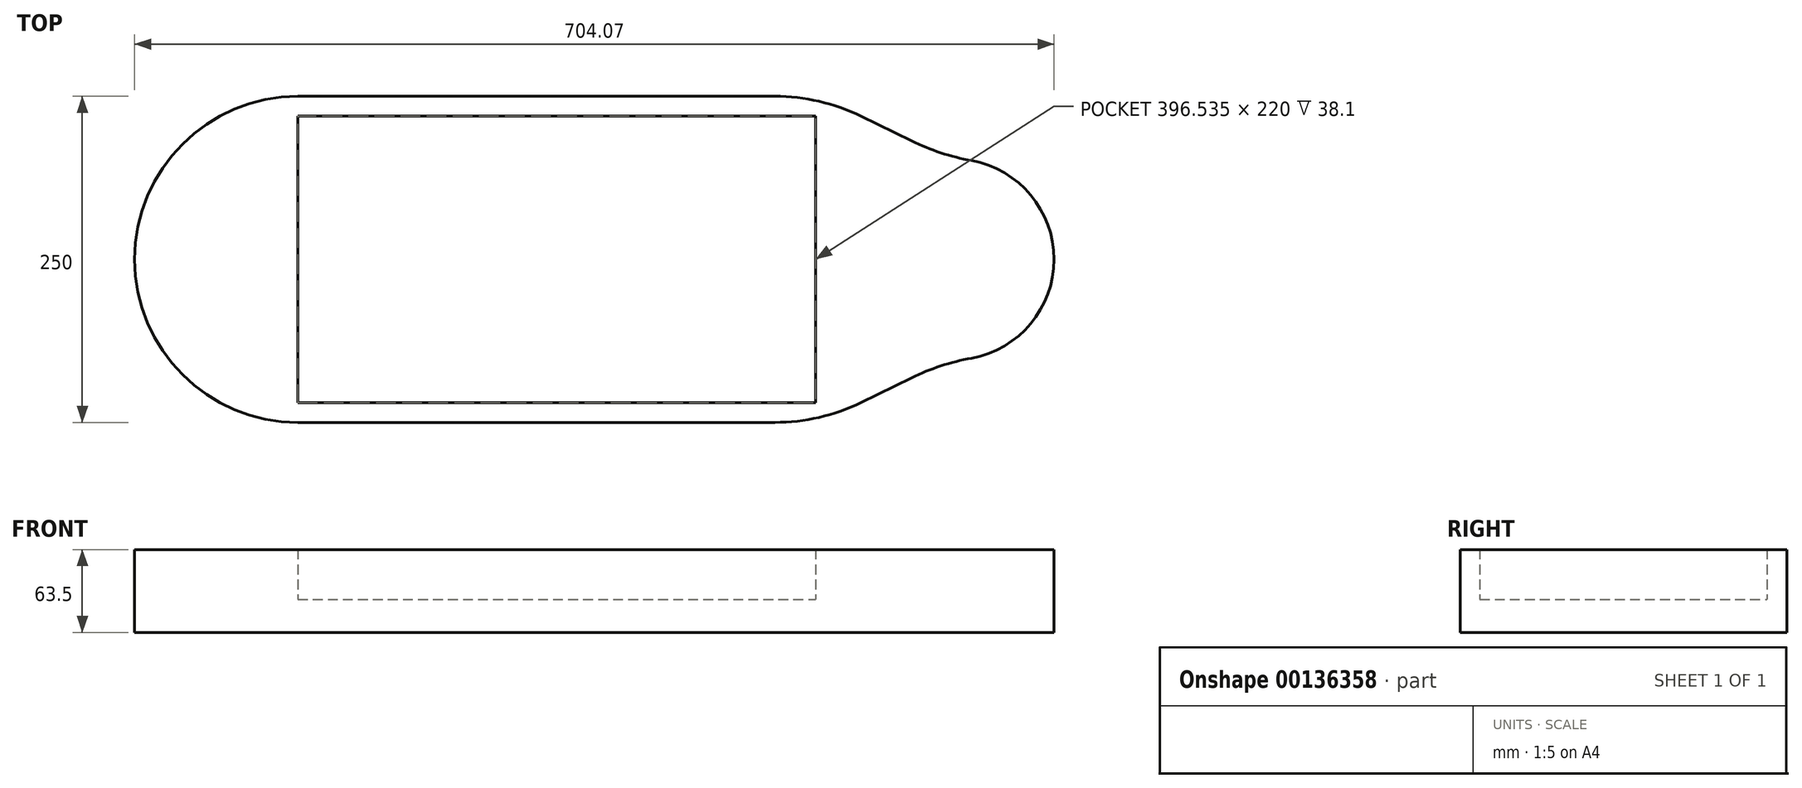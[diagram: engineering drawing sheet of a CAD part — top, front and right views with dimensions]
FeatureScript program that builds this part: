
annotation { "Feature Type Name" : "Feature", "Feature Type Description" : "" }
export const myFeature = defineFeature(function(context is Context, id is Id, definition is map)
    precondition{}
    {
        {
            var Q0;
            Q0=qCreatedBy(makeId("Top.planeOp"),FACE);
            var sketch = newSketch(context, id + "F0", { "sketchPlane" : qUnion([Q0])});
            skLineSegment(sketch, "E0", {"start": v(-202.42, 0) * mm, "end": v(197.58, 0) * mm});
            skLineSegment(sketch, "E1", {"start": v(-202.42, 250) * mm, "end": v(197.58, 250) * mm});
            skArc(sketch, "E2", {"start": v(-202.42, 250) * mm, "mid": v(-327.42, 125) * mm, "end": v(-202.42, 0) * mm});
            skLineSegment(sketch, "E3", {"start": v(-202.42, 125) * mm, "end": v(197.58, 125) * mm, "construction": true});
            skPoint(sketch, "E4.MirrorCS.start.orphan", {"position": v(197.58, 0) * mm});
            skArc(sketch, "E5", {"start": v(296.11, 48.09) * mm, "mid": v(376.65, 125) * mm, "end": v(296.11, 201.91) * mm});
            skLineSegment(sketch, "E6", {"start": v(197.58, 0) * mm, "end": v(296.11, 48.09) * mm});
            skLineSegment(sketch, "E7", {"start": v(197.58, 250) * mm, "end": v(296.11, 201.91) * mm});
            skSolve(sketch);
        }
        {
            var Q0;
            Q0=makeQuery(id+"F0.imprint","IMPRINT",FACE,{"disambiguationData":[TD([[makeQuery(id+"F0.imprint","IMPRINT",EDGE,{"derivedFrom":sQuery(id+"F0.wireOp",EDGE,"E0")}),1.0]])]});
            extrude(context, id + "F1", {"entities" : qUnion([Q0]), "depth" : 25.4 * mm});
        }
        {
            var Q0;
            Q0=makeQuery(id+"F1.opExtrude","CAP_FACE",FACE,{"disambiguationData":[OSD([sQuery(id+"F0.wireOp",EDGE,"E0"),sQuery(id+"F0.wireOp",EDGE,"E1"),sQuery(id+"F0.wireOp",EDGE,"E2"),sQuery(id+"F0.wireOp",EDGE,"E5"),sQuery(id+"F0.wireOp",EDGE,"E6"),sQuery(id+"F0.wireOp",EDGE,"E7")])],"isStart":false});
            var sketch = newSketch(context, id + "F2", { "sketchPlane" : qUnion([Q0])});
            skLineSegment(sketch, "E8.0", {"start": v(194.11, 235) * mm, "end": v(-202.42, 235) * mm});
            skLineSegment(sketch, "E8.1", {"start": v(-202.42, 15) * mm, "end": v(194.11, 15) * mm});
            skLineSegment(sketch, "E9", {"start": v(194.11, 15) * mm, "end": v(194.11, 235) * mm});
            skLineSegment(sketch, "E10", {"start": v(-202.42, 15) * mm, "end": v(-202.42, 235) * mm});
            skSolve(sketch);
        }
        {
            var Q0;
            Q0=makeQuery(id+"F2.imprint","IMPRINT",FACE,{"disambiguationData":[TD([[makeQuery(id+"F2.imprint","IMPRINT",EDGE,{"derivedFrom":sQuery(id+"F2.wireOp",EDGE,"E8.0")}),-1.0]])]});
            extrude(context, id + "F3", {"entities" : qUnion([Q0]), "operationType" : NewBodyOperationType.ADD, "depth" : 38.1 * mm});
        }
        {
            var Q0;
            {var subQ0=sQuery(id+"F0.wireOp",EDGE,"E7");var subQ1=sQuery(id+"F0.wireOp",EDGE,"E5");Q0=makeQuery(id+"F3.boolean.opBoolean","MERGE",EDGE,{"derivedFrom":[makeQuery(id+"F1.opExtrude","SWEPT_EDGE",EDGE,{"disambiguationData":[OSD([subQ1,subQ0])]}),makeQuery(id+"F3.opExtrude","SWEPT_EDGE",EDGE,{"disambiguationData":[OSD([subQ1,subQ0])]})]});}
            fillet(context, id + "F4", {"entities" : qUnion([Q0]), "radius" : 177.37 * mm, "tangentPropagation" : true, "allowEdgeOverflow" : false});
        }
        {
            var Q0;
            {var subQ0=sQuery(id+"F0.wireOp",EDGE,"E7");var subQ1=sQuery(id+"F0.wireOp",EDGE,"E1");Q0=makeQuery(id+"F3.boolean.opBoolean","MERGE",EDGE,{"derivedFrom":[makeQuery(id+"F1.opExtrude","SWEPT_EDGE",EDGE,{"disambiguationData":[OSD([subQ1,subQ0])]}),makeQuery(id+"F3.opExtrude","SWEPT_EDGE",EDGE,{"disambiguationData":[OSD([subQ1,subQ0])]})]});}
            fillet(context, id + "F5", {"entities" : qUnion([Q0]), "radius" : 149.72 * mm, "tangentPropagation" : true, "allowEdgeOverflow" : false});
        }
        {
            var Q0;
            {var subQ0=sQuery(id+"F0.wireOp",EDGE,"E6");var subQ1=sQuery(id+"F0.wireOp",EDGE,"E5");Q0=makeQuery(id+"F3.boolean.opBoolean","MERGE",EDGE,{"derivedFrom":[makeQuery(id+"F1.opExtrude","SWEPT_EDGE",EDGE,{"disambiguationData":[OSD([subQ1,subQ0])]}),makeQuery(id+"F3.opExtrude","SWEPT_EDGE",EDGE,{"disambiguationData":[OSD([subQ1,subQ0])]})]});}
            fillet(context, id + "F6", {"entities" : qUnion([Q0]), "radius" : 177.37 * mm, "tangentPropagation" : true, "allowEdgeOverflow" : false});
        }
        {
            var Q0;
            {var subQ0=sQuery(id+"F0.wireOp",EDGE,"E6");var subQ1=sQuery(id+"F0.wireOp",EDGE,"E0");Q0=makeQuery(id+"F3.boolean.opBoolean","MERGE",EDGE,{"derivedFrom":[makeQuery(id+"F1.opExtrude","SWEPT_EDGE",EDGE,{"disambiguationData":[OSD([subQ1,subQ0])]}),makeQuery(id+"F3.opExtrude","SWEPT_EDGE",EDGE,{"disambiguationData":[OSD([subQ1,subQ0])]})]});}
            fillet(context, id + "F7", {"entities" : qUnion([Q0]), "radius" : 149.73 * mm, "tangentPropagation" : true, "allowEdgeOverflow" : false});
        }
    });
